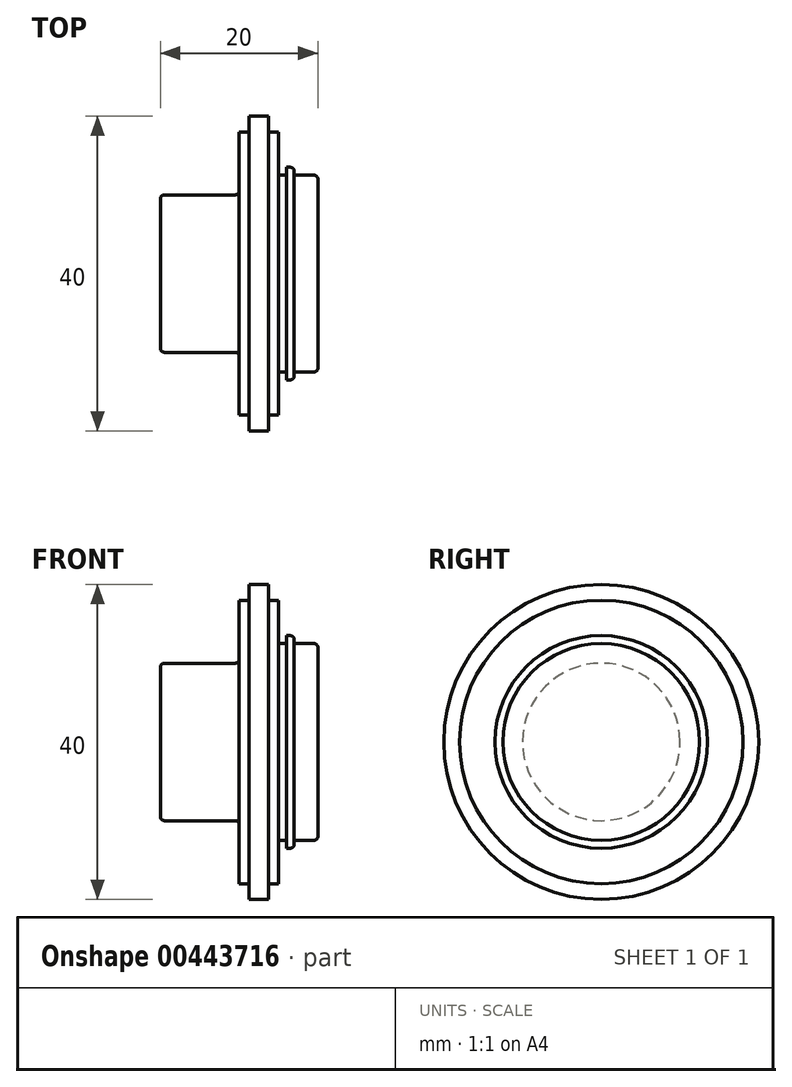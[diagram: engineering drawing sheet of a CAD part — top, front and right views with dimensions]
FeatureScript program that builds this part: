
annotation { "Feature Type Name" : "Feature", "Feature Type Description" : "" }
export const myFeature = defineFeature(function(context is Context, id is Id, definition is map)
    precondition{}
    {
        {
            var Q0;
            Q0=qCreatedBy(makeId("Front.planeOp"),FACE);
            var sketch = newSketch(context, id + "F0", { "sketchPlane" : qUnion([Q0])});
            skLineSegment(sketch, "E0", {"start": v(0, 0) * mm, "end": v(-20, 0) * mm});
            skLineSegment(sketch, "E1", {"start": v(-20, 0) * mm, "end": v(-20, 10) * mm});
            skLineSegment(sketch, "E2", {"start": v(-20, 10) * mm, "end": v(-10, 10) * mm});
            skLineSegment(sketch, "E3", {"start": v(-10, 10) * mm, "end": v(-10, 18) * mm});
            skLineSegment(sketch, "E4", {"start": v(-10, 18) * mm, "end": v(-8.75, 18) * mm});
            skLineSegment(sketch, "E5", {"start": v(-8.75, 18) * mm, "end": v(-8.75, 20) * mm});
            skLineSegment(sketch, "E6", {"start": v(-8.75, 20) * mm, "end": v(-6.25, 20) * mm});
            skLineSegment(sketch, "E7", {"start": v(-6.25, 20) * mm, "end": v(-6.25, 18) * mm});
            skLineSegment(sketch, "E8", {"start": v(-6.25, 18) * mm, "end": v(-5, 18) * mm});
            skLineSegment(sketch, "E9", {"start": v(-5, 18) * mm, "end": v(-5, 12.5) * mm});
            skLineSegment(sketch, "E10", {"start": v(-5, 12.5) * mm, "end": v(-4, 12.5) * mm});
            skLineSegment(sketch, "E11", {"start": v(-4, 12.5) * mm, "end": v(-4, 13.5) * mm});
            skLineSegment(sketch, "E12", {"start": v(-4, 13.5) * mm, "end": v(-3, 13.5) * mm});
            skLineSegment(sketch, "E13", {"start": v(-3, 13.5) * mm, "end": v(-3, 12.5) * mm});
            skLineSegment(sketch, "E14", {"start": v(-3, 12.5) * mm, "end": v(0, 12.5) * mm});
            skLineSegment(sketch, "E15", {"start": v(0, 12.5) * mm, "end": v(0, 0) * mm});
            skSolve(sketch);
        }
        {
            var Q0;
            Q0=makeQuery(id+"F0.imprint","IMPRINT",FACE,{"disambiguationData":[TD([[makeQuery(id+"F0.imprint","IMPRINT",EDGE,{"derivedFrom":sQuery(id+"F0.wireOp",EDGE,"E0")}),-1.0]])]});
            var Q1;
            Q1=sQuery(id+"F0.wireOp",EDGE,"E0");
            revolve(context, id + "F1", {"entities" : qUnion([Q0]), "axis" : qUnion([Q1]), "revolveType" : RevolveType.FULL});
        }
        {
            var Q0;
            Q0=makeQuery(id+"F1.opRevolve","SWEPT_FACE",FACE,{"disambiguationData":[OSD([sQuery(id+"F0.wireOp",EDGE,"E2")])]});
            var Q1;
            Q1=makeQuery(id+"F1.opRevolve","SWEPT_EDGE",EDGE,{"disambiguationData":[OSD([sQuery(id+"F0.wireOp",EDGE,"E12"),sQuery(id+"F0.wireOp",EDGE,"E13")])]});
            var Q2;
            Q2=makeQuery(id+"F1.opRevolve","SWEPT_FACE",FACE,{"disambiguationData":[OSD([sQuery(id+"F0.wireOp",EDGE,"E15")])]});
            fillet(context, id + "F2", {"entities" : qUnion([Q0, Q1, Q2]), "radius" : 0.5 * mm, "tangentPropagation" : true, "allowEdgeOverflow" : false});
        }
    });
